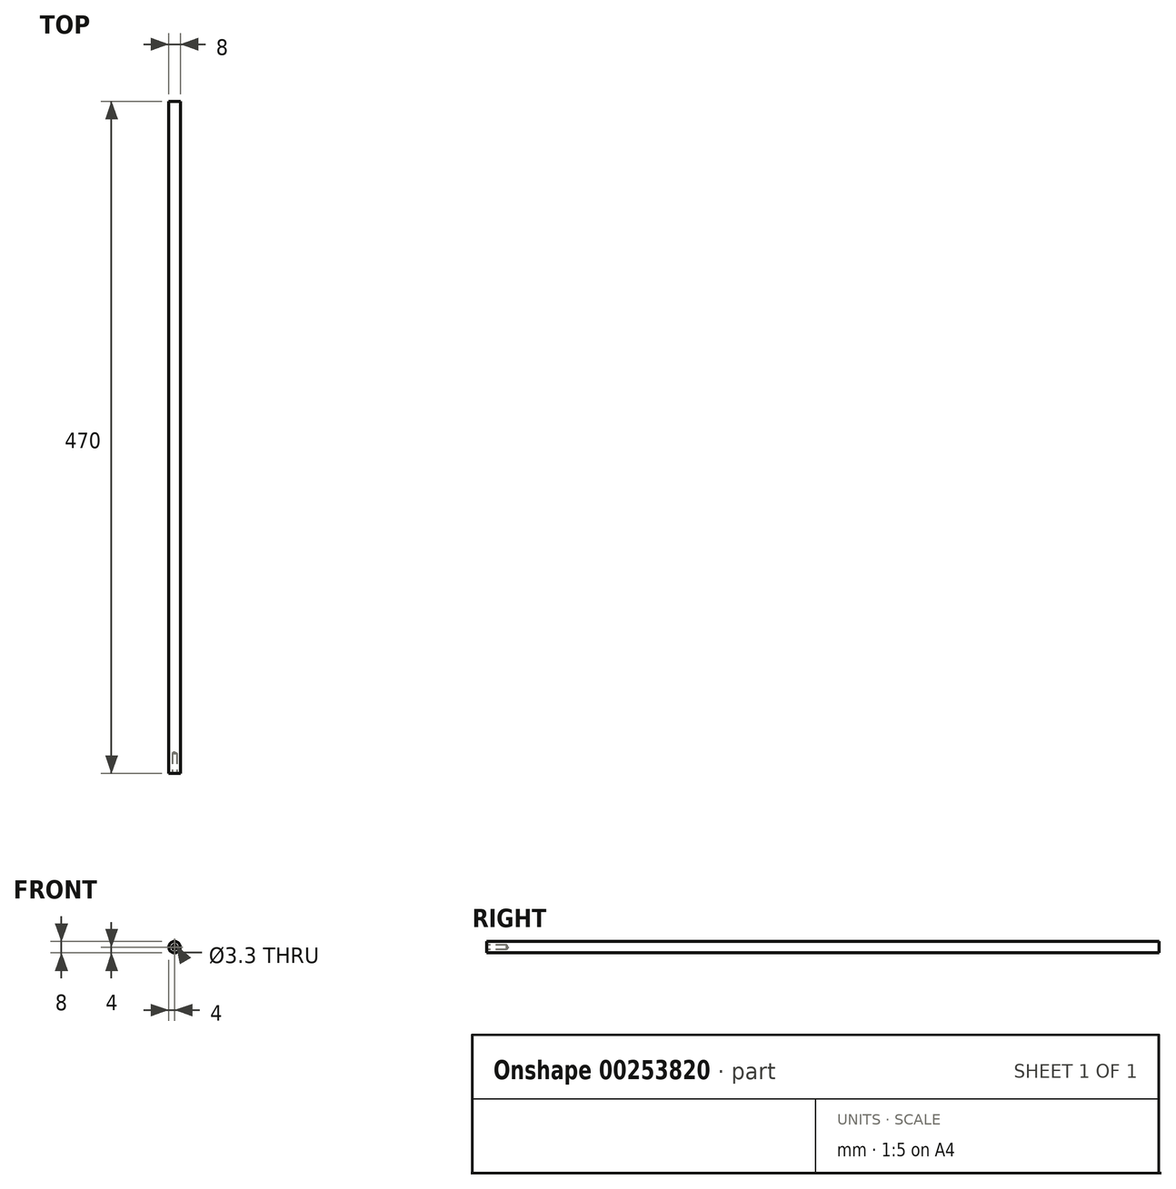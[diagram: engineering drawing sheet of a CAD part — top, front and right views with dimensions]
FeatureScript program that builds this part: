
annotation { "Feature Type Name" : "Feature", "Feature Type Description" : "" }
export const myFeature = defineFeature(function(context is Context, id is Id, definition is map)
    precondition{}
    {
        {
            var Q0;
            Q0=qCreatedBy(makeId("Front.planeOp"),FACE);
            var sketch = newSketch(context, id + "F0", { "sketchPlane" : qUnion([Q0])});
            skCircle(sketch, "E0", {"center": v(0, 0) * mm, "radius": 4 * mm});
            skSolve(sketch);
        }
        {
            var Q0;
            Q0=makeQuery(id+"F0.imprint","IMPRINT",FACE,{"disambiguationData":[TD([[makeQuery(id+"F0.imprint","IMPRINT",EDGE,{"derivedFrom":sQuery(id+"F0.wireOp",EDGE,"E0")}),1.0]])]});
            extrude(context, id + "F1", {"entities" : qUnion([Q0]), "offsetDistance" : 25 * mm, "depth" : 470 * mm});
        }
        {
            var Q0;
            Q0=makeQuery(id+"F1.opExtrude","CAP_FACE",FACE,{"disambiguationData":[OSD([sQuery(id+"F0.wireOp",EDGE,"E0")])],"isStart":false});
            var sketch = newSketch(context, id + "F2", { "sketchPlane" : qUnion([Q0])});
            skPoint(sketch, "E1", {"position": v(0, 0) * mm});
            skSolve(sketch);
        }
        {
            var Q0;
            Q0=sQuery(id+"F2.wireOp",VERTEX,"E1");
            var Q1;
            Q1=makeQuery(id+"F1.opExtrude","SWEPT_BODY",BODY,{"disambiguationData":[OSD([sQuery(id+"F0.wireOp",EDGE,"E0")])]});
            hole(context, id + "F3", {"style" : HoleStyle.SIMPLE, "endStyle" : HoleEndStyle.BLIND, "standardTappedOrClearance" : lookupTablePath({ "standard" : "ISO", "engagement" : "75%", "pitch" : "0.7 mm", "size" : "M4", "type" : "Tapped" }), "standardBlindInLast" : lookupTablePath({ "standard" : "ISO", "fit" : "Normal", "engagement" : "75%", "pitch" : "0.7 mm", "size" : "M4", "type" : "Clearance & tapped" }), "holeDiameter" : 3.3 * mm, "majorDiameter" : 4 * mm, "showTappedDepth" : true, "holeDepth" : 14.1 * mm, "isTappedThrough" : true, "tappedDepth" : 12 * mm, "tapClearance" : 3, "locations" : qUnion([Q0]), "scope" : qUnion([Q1])});
        }
    });
